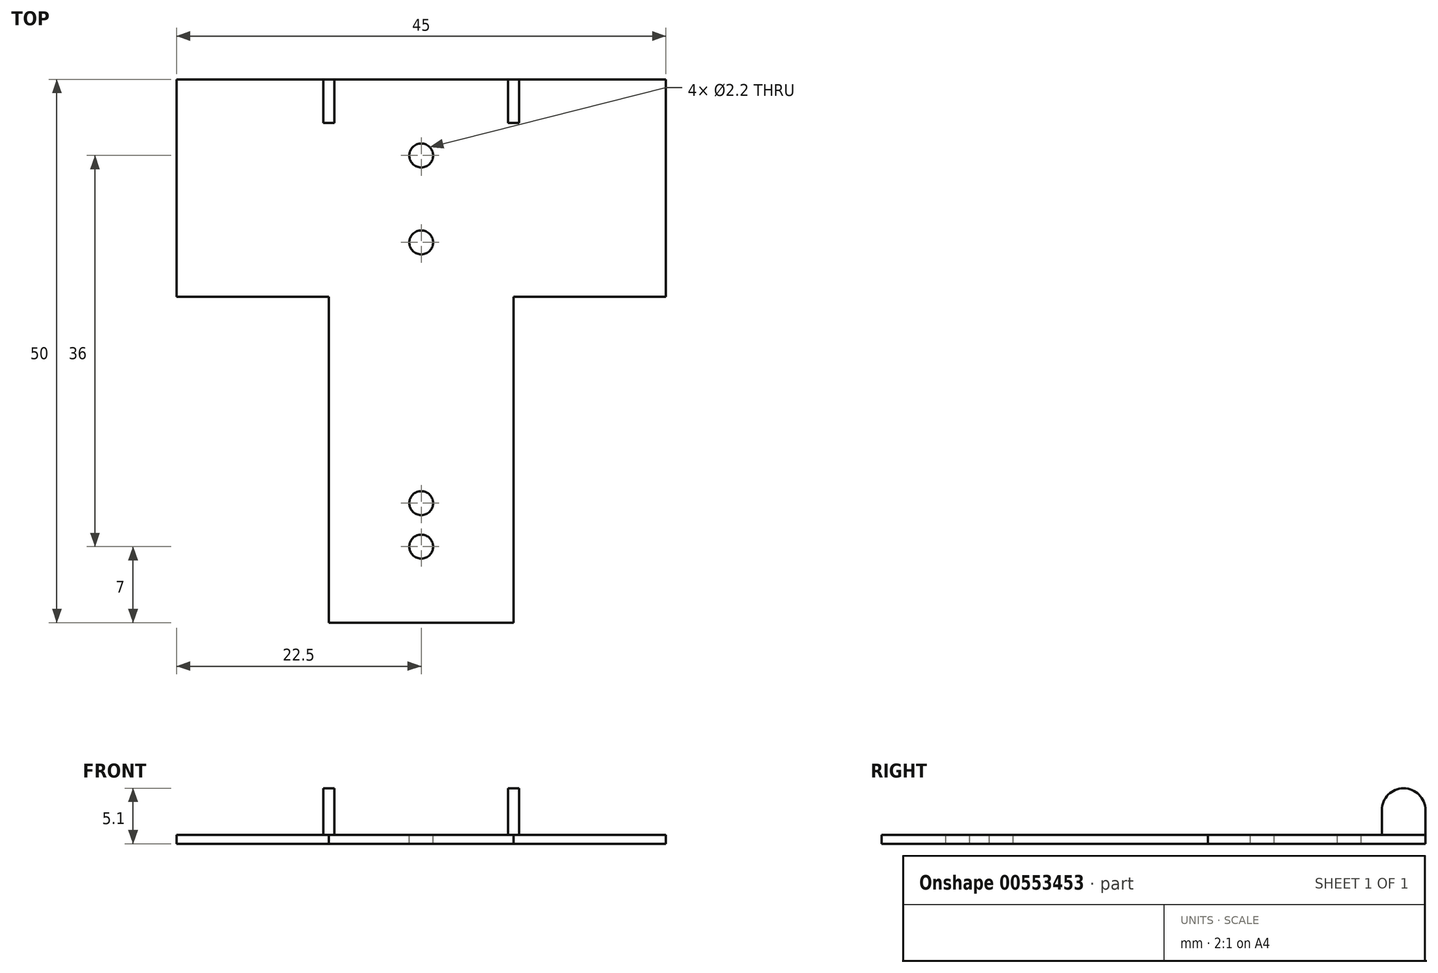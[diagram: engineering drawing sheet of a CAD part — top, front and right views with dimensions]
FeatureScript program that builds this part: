
annotation { "Feature Type Name" : "Feature", "Feature Type Description" : "" }
export const myFeature = defineFeature(function(context is Context, id is Id, definition is map)
    precondition{}
    {
        {
            var Q0;
            Q0=qCreatedBy(makeId("Top.planeOp"),FACE);
            var sketch = newSketch(context, id + "F0", { "sketchPlane" : qUnion([Q0])});
            skLineSegment(sketch, "E0", {"start": v(-8.5, -27.5) * mm, "end": v(-8.5, 2.5) * mm});
            skLineSegment(sketch, "E1", {"start": v(-8.5, 2.5) * mm, "end": v(-22.5, 2.5) * mm});
            skLineSegment(sketch, "E2", {"start": v(-22.5, 2.5) * mm, "end": v(-22.5, 22.5) * mm});
            skLineSegment(sketch, "E3", {"start": v(-22.5, 22.5) * mm, "end": v(22.5, 22.5) * mm});
            skLineSegment(sketch, "E4", {"start": v(22.5, 22.5) * mm, "end": v(22.5, 2.5) * mm});
            skLineSegment(sketch, "E5", {"start": v(22.5, 2.5) * mm, "end": v(8.5, 2.5) * mm});
            skLineSegment(sketch, "E6", {"start": v(8.5, 2.5) * mm, "end": v(8.5, -27.5) * mm});
            skLineSegment(sketch, "E7", {"start": v(8.5, -27.5) * mm, "end": v(-8.5, -27.5) * mm});
            skSolve(sketch);
        }
        {
            var Q0;
            Q0 = qSketchRegion(id + "F0", true);
            extrude(context, id + "F1", {"entities" : qUnion([Q0]), "depth" : 0.8 * mm, "offsetDistance" : 25 * mm});
        }
        {
            var Q0;
            Q0=qCreatedBy(makeId("Right.planeOp"),FACE);
            cPlane(context, id + "F2", {"entities" : qUnion([Q0]), "cplaneType" : CPlaneType.OFFSET, "offset" : 8 * mm, "width" : 150 * mm, "height" : 150 * mm});
        }
        {
            var Q0;
            Q0=qCreatedBy(id+"F2.planeOp",FACE);
            var sketch = newSketch(context, id + "F3", { "sketchPlane" : qUnion([Q0])});
            skLineSegment(sketch, "E8", {"start": v(18.5, 0.8) * mm, "end": v(18.5, 3.1) * mm});
            skLineSegment(sketch, "E9", {"start": v(18.5, 0.8) * mm, "end": v(22.5, 0.8) * mm});
            skLineSegment(sketch, "E10", {"start": v(22.5, 0.8) * mm, "end": v(22.5, 3.1) * mm});
            skLineSegment(sketch, "E11", {"start": v(-22.6, 3.1) * mm, "end": v(-28.17, 3.1) * mm, "construction": true});
            skArc(sketch, "E12", {"start": v(22.5, 3.1) * mm, "mid": v(20.5, 5.1) * mm, "end": v(18.5, 3.1) * mm});
            skSolve(sketch);
        }
        {
            var Q0;
            Q0 = qSketchRegion(id + "F3", true);
            extrude(context, id + "F4", {"entities" : qUnion([Q0]), "depth" : 1 * mm, "offsetDistance" : 25 * mm});
        }
        {
            var Q0;
            Q0=makeQuery(id+"F4.opExtrude","SWEPT_BODY",BODY,{"disambiguationData":[OSD([sQuery(id+"F3.wireOp",EDGE,"E8"),sQuery(id+"F3.wireOp",EDGE,"E9"),sQuery(id+"F3.wireOp",EDGE,"E10"),sQuery(id+"F3.wireOp",EDGE,"E12")])]});
            var Q1;
            Q1=qCreatedBy(makeId("Right.planeOp"),FACE);
            mirror(context, id + "F5", {"operationType" : NewBodyOperationType.ADD, "entities" : qUnion([Q0]), "mirrorPlane" : qUnion([Q1])});
        }
        {
            var Q0;
            Q0=makeQuery(id+"F1.opExtrude","CAP_FACE",FACE,{"disambiguationData":[OSD([sQuery(id+"F0.wireOp",EDGE,"E0"),sQuery(id+"F0.wireOp",EDGE,"E1"),sQuery(id+"F0.wireOp",EDGE,"E2"),sQuery(id+"F0.wireOp",EDGE,"E3"),sQuery(id+"F0.wireOp",EDGE,"E4"),sQuery(id+"F0.wireOp",EDGE,"E5"),sQuery(id+"F0.wireOp",EDGE,"E6"),sQuery(id+"F0.wireOp",EDGE,"E7")])],"isStart":false});
            var sketch = newSketch(context, id + "F6", { "sketchPlane" : qUnion([Q0])});
            skCircle(sketch, "E13", {"center": v(0, 15.5) * mm, "radius": 1.1 * mm});
            skCircle(sketch, "E14", {"center": v(0, 7.5) * mm, "radius": 1.1 * mm});
            skCircle(sketch, "E15", {"center": v(0, -16.5) * mm, "radius": 1.1 * mm});
            skCircle(sketch, "E16", {"center": v(0, -20.5) * mm, "radius": 1.1 * mm});
            skSolve(sketch);
        }
        {
            var Q0;
            Q0 = qSketchRegion(id + "F6", true);
            extrude(context, id + "F7", {"entities" : qUnion([Q0]), "operationType" : NewBodyOperationType.REMOVE, "endBound" : BoundingType.THROUGH_ALL, "oppositeDirection" : true, "depth" : 25 * mm, "offsetDistance" : 25 * mm});
        }
    });
